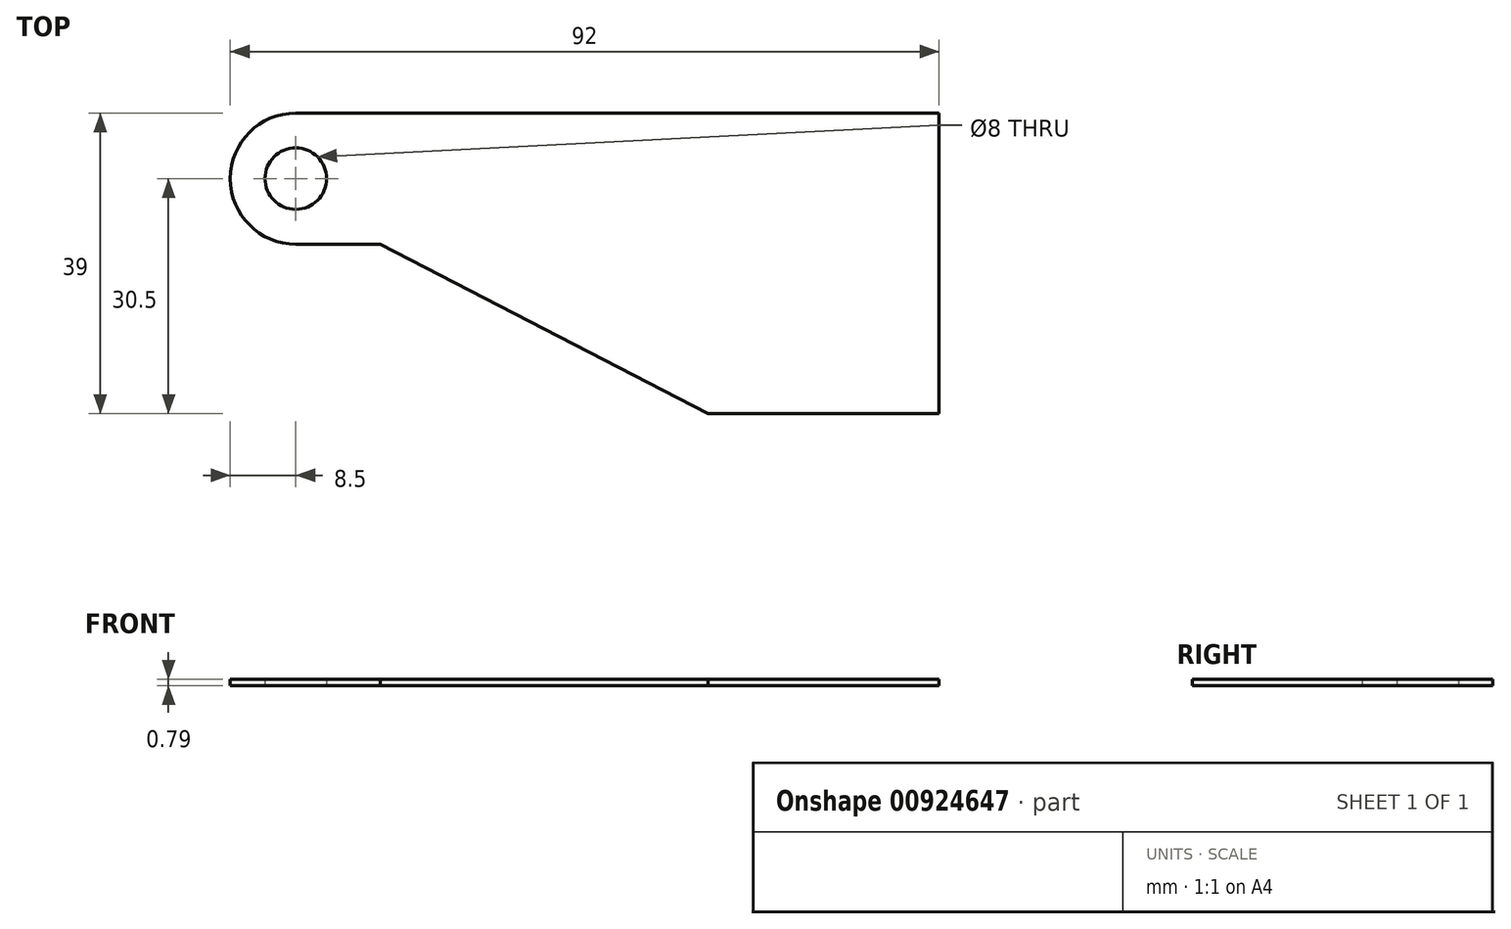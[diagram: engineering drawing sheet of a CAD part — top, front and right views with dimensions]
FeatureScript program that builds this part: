
annotation { "Feature Type Name" : "Feature", "Feature Type Description" : "" }
export const myFeature = defineFeature(function(context is Context, id is Id, definition is map)
    precondition{}
    {
        {
            var Q0;
            Q0=qCreatedBy(makeId("Top.planeOp"),FACE);
            var sketch = newSketch(context, id + "F0", { "sketchPlane" : qUnion([Q0])});
            skCircle(sketch, "E0", {"center": v(0, 0) * mm, "radius": 4 * mm});
            skArc(sketch, "E1", {"start": v(0, 8.5) * mm, "mid": v(-8.5, 0) * mm, "end": v(0, -8.5) * mm});
            skLineSegment(sketch, "E2", {"start": v(0, 8.5) * mm, "end": v(83.5, 8.5) * mm});
            skLineSegment(sketch, "E3", {"start": v(83.5, 8.5) * mm, "end": v(83.5, -30.5) * mm});
            skLineSegment(sketch, "E4", {"start": v(83.5, -30.5) * mm, "end": v(53.5, -30.5) * mm});
            skLineSegment(sketch, "E5", {"start": v(53.5, -30.5) * mm, "end": v(11, -8.5) * mm});
            skLineSegment(sketch, "E6", {"start": v(11, -8.5) * mm, "end": v(0, -8.5) * mm});
            skPoint(sketch, "E7.start.orphan", {"position": v(8.5, 0) * mm});
            skSolve(sketch);
        }
        {
            var Q0;
            Q0 = qSketchRegion(id + "F0", true);
            extrude(context, id + "F1", {"entities" : qUnion([Q0]), "depth" : 0.8 * mm, "offsetDistance" : 25 * mm});
        }
    });
